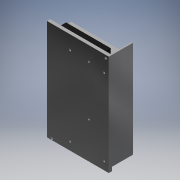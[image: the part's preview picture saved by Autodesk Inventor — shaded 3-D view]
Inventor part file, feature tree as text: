
AUTODESK INVENTOR PART (.ipt)
format: ipt  version: 2018 (Build 220112000, 112)  size: 169,472 bytes
history: native  units: mm
features: extrude x6, sketch x6
ambient origin geometry x8: Origin, YZ Plane, XZ Plane, XY Plane, X Axis, Y Axis, Z Axis, Center Point
bodies: Solid1 (feature_tree)
feature tree (12):
  extrude  "Extrusion1"  Depth=158.0mm
  extrude  "Extrusion2"  Depth=5.0mm
  extrude  "Extrusion3"  Depth=89.5mm
  extrude  "Extrusion4"  Depth=4.5mm
  extrude  "Extrusion5"  Depth=5.0mm TaperAngle=0.0deg
  extrude  "Extrusion6"  Depth=20.0mm
  sketch  "Sketch1"  dims[d0=97.0mm d1=158.0mm]
  sketch  "Sketch2"  dims[d2=5.0mm d3=0.0mm d4=3.5mm]
  sketch  "Sketch3"  dims[d5=155.75mm d6=89.5mm]
  sketch  "Sketch4"  dims[d7=3.5mm d8=4.5mm]
  sketch  "Sketch5"  dims[d9=5.0mm d10=5.0mm d11=0.0mm]
  sketch  "Sketch6"  dims[d12=6.0mm d13=20.0mm d14=33.0mm d15=0.0mm d16=2.0mm d17=20.0mm d18=0.0mm d19=70.0mm d20=10.0mm d21=7.0mm d22=15.0mm d23=0.0mm d24=3.2mm d25=3.2mm d26=3.2mm d27=3.2mm d28=3.2mm d29=7.5mm d30=25.4mm d31=22.5mm d32=31.5mm d33=61.0mm d34=21.4mm d35=120.0mm d36=3.2mm d37=78.0mm d38=2.0mm d39=0.0mm]
